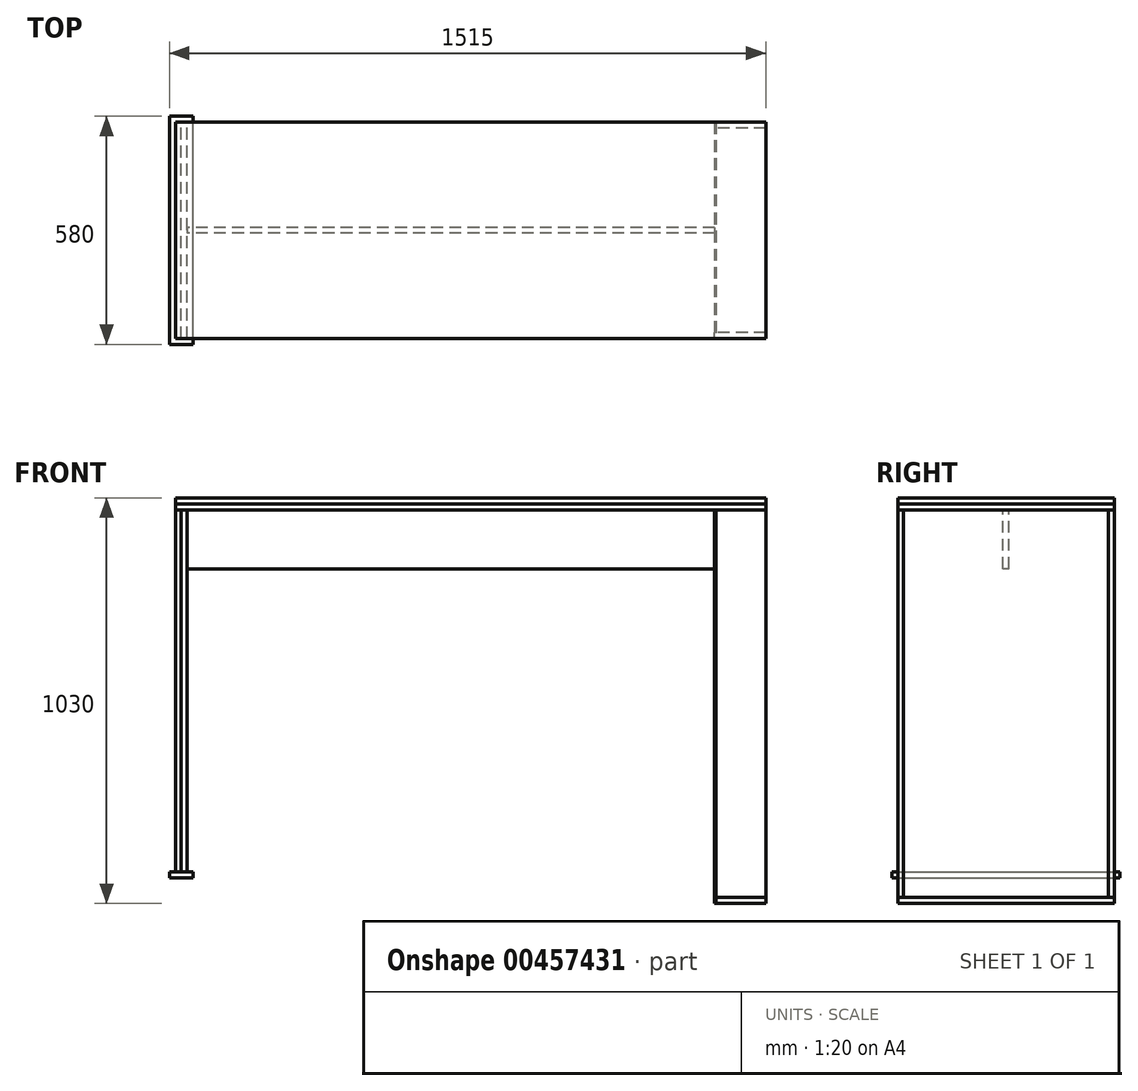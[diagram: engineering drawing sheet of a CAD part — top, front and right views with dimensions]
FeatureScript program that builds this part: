
annotation { "Feature Type Name" : "Feature", "Feature Type Description" : "" }
export const myFeature = defineFeature(function(context is Context, id is Id, definition is map)
    precondition{}
    {
        {
            var Q0;
            Q0=qCreatedBy(makeId("Top.planeOp"),FACE);
            var sketch = newSketch(context, id + "F0", { "sketchPlane" : qUnion([Q0])});
            skLineSegment(sketch, "E0.bottom", {"start": v(750, -275) * mm, "end": v(-750, -275) * mm});
            skLineSegment(sketch, "E0.top", {"start": v(750, 275) * mm, "end": v(-750, 275) * mm});
            skLineSegment(sketch, "E0.left", {"start": v(750, -275) * mm, "end": v(750, 275) * mm});
            skLineSegment(sketch, "E0.right", {"start": v(-750, -275) * mm, "end": v(-750, 275) * mm});
            skPoint(sketch, "E0.middle", {"position": v(0, 0) * mm});
            skSolve(sketch);
        }
        {
            var Q0;
            Q0 = qSketchRegion(id + "F0", true);
            extrude(context, id + "F1", {"entities" : qUnion([Q0]), "depth" : 15 * mm});
        }
        {
            var Q0;
            Q0=makeQuery(id+"F1.opExtrude","CAP_FACE",FACE,{"disambiguationData":[OSD([sQuery(id+"F0.wireOp",EDGE,"E0.bottom"),sQuery(id+"F0.wireOp",EDGE,"E0.top"),sQuery(id+"F0.wireOp",EDGE,"E0.left"),sQuery(id+"F0.wireOp",EDGE,"E0.right")])],"isStart":false});
            extrude(context, id + "F2", {"entities" : qUnion([Q0]), "depth" : 15 * mm});
        }
        {
            var Q0;
            Q0=makeQuery(id+"F1.opExtrude","CAP_FACE",FACE,{"disambiguationData":[OSD([sQuery(id+"F0.wireOp",EDGE,"E0.bottom"),sQuery(id+"F0.wireOp",EDGE,"E0.top"),sQuery(id+"F0.wireOp",EDGE,"E0.left"),sQuery(id+"F0.wireOp",EDGE,"E0.right")])],"isStart":true});
            var sketch = newSketch(context, id + "F3", { "sketchPlane" : qUnion([Q0])});
            skLineSegment(sketch, "E1.bottom", {"start": v(-750, 275) * mm, "end": v(-735, 275) * mm});
            skLineSegment(sketch, "E1.top", {"start": v(-750, -275) * mm, "end": v(-735, -275) * mm});
            skLineSegment(sketch, "E1.left", {"start": v(-750, 275) * mm, "end": v(-750, -275) * mm});
            skLineSegment(sketch, "E1.right", {"start": v(-735, 275) * mm, "end": v(-735, -275) * mm});
            skSolve(sketch);
        }
        {
            var Q0;
            Q0=makeQuery(id+"F3.imprint","IMPRINT",FACE,{"disambiguationData":[TD([[makeQuery(id+"F3.imprint","IMPRINT",EDGE,{"derivedFrom":sQuery(id+"F3.wireOp",EDGE,"E1.bottom")}),1.0]])]});
            extrude(context, id + "F4", {"entities" : qUnion([Q0]), "depth" : 920 * mm});
        }
        {
            var Q0;
            Q0=makeQuery(id+"F4.opExtrude","SWEPT_FACE",FACE,{"disambiguationData":[OSD([sQuery(id+"F3.wireOp",EDGE,"E1.right")])]});
            var Q1;
            Q1=sQuery(id+"F7mP7dXpb9NDCW2_4.wireOp",EDGE,"6nfuIFvM-9UVF-QKha-oN4r-lZPG21bFVyJS.top");
            extrude(context, id + "F5", {"entities" : qUnion([Q0]), "surfaceEntities" : qUnion([Q1]), "depth" : 15 * mm});
        }
        {
            var Q0;
            Q0=makeQuery(id+"F1.opExtrude","CAP_FACE",FACE,{"disambiguationData":[OSD([sQuery(id+"F0.wireOp",EDGE,"E0.bottom"),sQuery(id+"F0.wireOp",EDGE,"E0.top"),sQuery(id+"F0.wireOp",EDGE,"E0.left"),sQuery(id+"F0.wireOp",EDGE,"E0.right")])],"isStart":true});
            var sketch = newSketch(context, id + "F6", { "sketchPlane" : qUnion([Q0])});
            skLineSegment(sketch, "E2.bottom", {"start": v(750, 275) * mm, "end": v(620, 275) * mm});
            skLineSegment(sketch, "E2.top", {"start": v(750, 260) * mm, "end": v(620, 260) * mm});
            skLineSegment(sketch, "E2.left", {"start": v(750, 275) * mm, "end": v(750, 260) * mm});
            skLineSegment(sketch, "E2.right", {"start": v(620, 275) * mm, "end": v(620, 260) * mm});
            skLineSegment(sketch, "E3.MirrorCS", {"start": v(750, -260) * mm, "end": v(620, -260) * mm});
            skLineSegment(sketch, "E4.MirrorCS", {"start": v(750, -275) * mm, "end": v(620, -275) * mm});
            skLineSegment(sketch, "E5.MirrorCS", {"start": v(620, -275) * mm, "end": v(620, -260) * mm});
            skLineSegment(sketch, "E6.MirrorCS", {"start": v(750, -275) * mm, "end": v(750, -260) * mm});
            skSolve(sketch);
        }
        {
            var Q0;
            Q0 = qSketchRegion(id + "F6", true);
            extrude(context, id + "F7", {"entities" : qUnion([Q0]), "depth" : 985 * mm});
        }
        {
            var Q0;
            Q0=makeQuery(id+"F7.opExtrude","CAP_FACE",FACE,{"disambiguationData":[OSD([sQuery(id+"F6.wireOp",EDGE,"E3.MirrorCS"),sQuery(id+"F6.wireOp",EDGE,"E4.MirrorCS"),sQuery(id+"F6.wireOp",EDGE,"E5.MirrorCS"),sQuery(id+"F6.wireOp",EDGE,"E6.MirrorCS")])],"isStart":false});
            var sketch = newSketch(context, id + "F8", { "sketchPlane" : qUnion([Q0])});
            skLineSegment(sketch, "E7.bottom", {"start": v(620, -275) * mm, "end": v(750, -275) * mm});
            skLineSegment(sketch, "E7.top", {"start": v(620, 275) * mm, "end": v(750, 275) * mm});
            skLineSegment(sketch, "E7.left", {"start": v(620, -275) * mm, "end": v(620, 275) * mm});
            skLineSegment(sketch, "E7.right", {"start": v(750, -275) * mm, "end": v(750, 275) * mm});
            skSolve(sketch);
        }
        {
            var Q0;
            Q0 = qSketchRegion(id + "F8", true);
            extrude(context, id + "F9", {"entities" : qUnion([Q0]), "depth" : 15 * mm});
        }
        {
            var Q0;
            Q0=makeQuery(id+"F1.opExtrude","CAP_FACE",FACE,{"disambiguationData":[OSD([sQuery(id+"F0.wireOp",EDGE,"E0.bottom"),sQuery(id+"F0.wireOp",EDGE,"E0.top"),sQuery(id+"F0.wireOp",EDGE,"E0.left"),sQuery(id+"F0.wireOp",EDGE,"E0.right")])],"isStart":true});
            var sketch = newSketch(context, id + "F10", { "sketchPlane" : qUnion([Q0])});
            skLineSegment(sketch, "E8.bottom", {"start": v(620, -275) * mm, "end": v(623, -275) * mm});
            skLineSegment(sketch, "E8.top", {"start": v(620, 275) * mm, "end": v(623, 275) * mm});
            skLineSegment(sketch, "E8.left", {"start": v(620, -275) * mm, "end": v(620, 275) * mm});
            skLineSegment(sketch, "E8.right", {"start": v(623, -275) * mm, "end": v(623, 275) * mm});
            skSolve(sketch);
        }
        {
            var Q0;
            Q0 = qSketchRegion(id + "F10", true);
            extrude(context, id + "F11", {"entities" : qUnion([Q0]), "depth" : 1000 * mm});
        }
        {
            var Q0;
            Q0=makeQuery(id+"F1.opExtrude","CAP_FACE",FACE,{"disambiguationData":[OSD([sQuery(id+"F0.wireOp",EDGE,"E0.bottom"),sQuery(id+"F0.wireOp",EDGE,"E0.top"),sQuery(id+"F0.wireOp",EDGE,"E0.left"),sQuery(id+"F0.wireOp",EDGE,"E0.right")])],"isStart":true});
            var sketch = newSketch(context, id + "F12", { "sketchPlane" : qUnion([Q0])});
            skLineSegment(sketch, "E9.bottom", {"start": v(620, -7.5) * mm, "end": v(-720, -7.5) * mm});
            skLineSegment(sketch, "E9.top", {"start": v(620, 7.5) * mm, "end": v(-720, 7.5) * mm});
            skLineSegment(sketch, "E9.left", {"start": v(620, -7.5) * mm, "end": v(620, 7.5) * mm});
            skLineSegment(sketch, "E9.right", {"start": v(-720, -7.5) * mm, "end": v(-720, 7.5) * mm});
            skPoint(sketch, "E9.middle", {"position": v(-50, 0) * mm});
            skSolve(sketch);
        }
        {
            var Q0;
            Q0 = qSketchRegion(id + "F12", true);
            extrude(context, id + "F13", {"entities" : qUnion([Q0]), "depth" : 150 * mm});
        }
        {
            var Q0;
            {var subQ0=sQuery(id+"F3.wireOp",EDGE,"E1.right");Q0=makeQuery(id+"F5.opExtrude","SWEPT_FACE",FACE,{"disambiguationData":[OSD([subQ0]),TDD([makeQuery(id+"F4.opExtrude","CAP_EDGE",EDGE,{"disambiguationData":[OSD([subQ0])],"isStart":false})])]});}
            var sketch = newSketch(context, id + "F14", { "sketchPlane" : qUnion([Q0])});
            skLineSegment(sketch, "E10.bottom", {"start": v(-765, 290) * mm, "end": v(-705, 290) * mm});
            skLineSegment(sketch, "E10.top", {"start": v(-765, -290) * mm, "end": v(-705, -290) * mm});
            skLineSegment(sketch, "E10.left", {"start": v(-765, 290) * mm, "end": v(-765, -290) * mm});
            skLineSegment(sketch, "E10.right", {"start": v(-705, 290) * mm, "end": v(-705, -290) * mm});
            skPoint(sketch, "E10.middle", {"position": v(-735, 0) * mm});
            skSolve(sketch);
        }
        {
            var Q0;
            Q0 = qSketchRegion(id + "F14", true);
            extrude(context, id + "F15", {"entities" : qUnion([Q0]), "depth" : 15 * mm});
        }
    });
